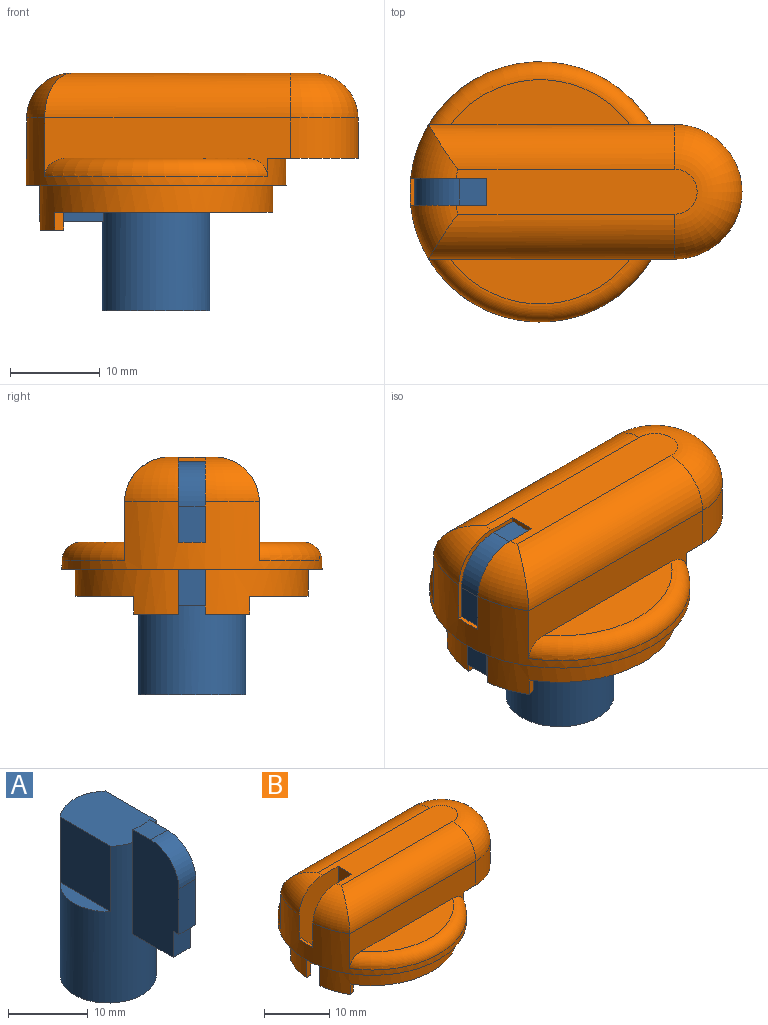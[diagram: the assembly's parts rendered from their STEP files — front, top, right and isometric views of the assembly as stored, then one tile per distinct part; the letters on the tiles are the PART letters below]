
ASSEMBLY  parts=2 mates=1
PART A: 19 faces, bbox 12x20x26 mm
  f0: plane 16x8.19mm, normal (-1,0,0), area 121.7mm2, adj f1,f3,f8,f9,f10,f14,f15,f16
  f1: plane 7x3mm, normal (0,-1,0), area 21mm2, adj f0,f2,f15,f16
  f2: plane 16x8.19mm, normal (1,0,0), area 121.7mm2, adj f1,f3,f8,f9,f10,f14,f15,f16
  f3: cylinder r=6mm len=24mm, axis (0,0,-1), area 660.5mm2, adj f0,f2,f6,f10,f11,f12,f13,f17
  f4: plane 10x4.4mm, normal (0,1,0), area 44mm2, adj f5,f6,f7
  f5: cylinder r=2.95mm len=10mm, axis (0,0,-1), area 135.7mm2, adj f4,f6,f7
  f6: plane 12x12mm, normal (0,0,-1), area 88.8mm2, adj f3,f4,f5
  f7: plane 5.9x4.92mm, normal (0,0,-1), area 24.3mm2, adj f4,f5
  f8: cylinder r=6mm len=3mm, axis (0,0,-1), area 6.1mm2, adj f0,f2,f9,f13
  f9: plane 3.19x3mm, normal (0,0,1), area 9.2mm2, adj f0,f2,f8,f16
  f10: plane 7.19x3mm, normal (0,0,-1), area 21.2mm2, adj f0,f2,f3,f14
  f11: plane 10x8.94mm, normal (1,0,0), area 89.4mm2, adj f3,f13,f18
  f12: plane 10x8.94mm, normal (-1,0,0), area 89.4mm2, adj f3,f13,f17
  f13: plane 12x8mm, normal (0,0,1), area 88.3mm2, adj f3,f8,f11,f12
  f14: plane 4x3mm, normal (0,-1,0), area 12mm2, adj f0,f2,f10,f15
  f15: plane 3x1mm, normal (0,0,-1), area 3mm2, adj f0,f1,f2,f14
  f16: cylinder r=5mm len=5mm, axis (-1,0,0), area 23.6mm2, adj f0,f1,f2,f9
  f17: plane 8.94x2mm, normal (0,0,1), area 12.4mm2, adj f3,f12
  f18: plane 8.94x2mm, normal (0,0,1), area 12.4mm2, adj f3,f11
PART B: 37 faces, bbox 38.1x31.4x17.5 mm
  f0: plane 3x2.5mm, normal (-1,0,0), area 7.5mm2, adj f16,f17,f18,f34
  f1: cylinder r=12mm len=4.67mm, axis (0,0,1), area 9.9mm2, adj f2,f7,f16,f19
  f2: plane 4.97x2.62mm, normal (0,0,-1), area 5.1mm2, adj f1,f6,f16,f19
  f3: plane 3x0.58mm, normal (0,0,1), area 1.5mm2, adj f10,f16,f17,f33
  f4: plane 20x5mm, normal (0,0,1), area 69.9mm2, adj f15,f36
  f5: cylinder r=11.6mm len=23.2mm, axis (0,0,-1), area 209.6mm2, adj f7,f11,f16,f17
  f6: cylinder r=13mm len=26mm, axis (0,0,-1), area 257.1mm2, adj f2,f7,f8,f16,f17,f19,f21,f22
  f7: plane 26x24.91mm, normal (0,0,-1), area 93.7mm2, adj f1,f5,f6,f16,f17,f19,f20,f21
  f8: plane 29x29mm, normal (0,0,-1), area 126.6mm2, adj f6,f10,f16,f17,f33
  f9: plane 20x5mm, normal (0,0,1), area 69.9mm2, adj f13,f35
  f10: cylinder r=14.5mm len=29mm, axis (0,0,-1), area 211.6mm2, adj f3,f8,f12,f13,f15,f16,f17,f23
  f11: plane 23.2x23.1mm, normal (0,0,-1), area 315.8mm2, adj f5,f16,f17,f28,f29,f30,f31,f32
  f12: plane 15x10.09mm, normal (0,0,-1), area 106mm2, adj f10,f13,f14,f15
  f13: plane 27.41x6.5mm, normal (0,-1,0), area 125.4mm2, adj f9,f10,f12,f14,f24,f35
  f14: cylinder r=7.5mm len=15mm, axis (0,0,-1), area 106mm2, adj f12,f13,f15,f26
  f15: plane 27.41x6.5mm, normal (0,1,0), area 125.4mm2, adj f4,f10,f12,f14,f27,f36
  f16: plane 17.5x8.61mm, normal (0,-1,0), area 106.7mm2, adj f0,f1,f2,f3,f5,f6,f7,f8
  f17: plane 17.5x8.61mm, normal (0,1,0), area 106.7mm2, adj f0,f3,f5,f6,f7,f8,f10,f11
  f18: plane 26.88x5mm, normal (0,0,1), area 121.1mm2, adj f0,f16,f17,f23,f24,f25,f26,f27
  f19: plane 2x0.99mm, normal (0.29,0.96,0), area 2.1mm2, adj f1,f2,f6,f7
  f20: cylinder r=12mm len=4.67mm, axis (0,0,1), area 9.9mm2, adj f7,f17,f21,f22
  f21: plane 2x0.99mm, normal (0.29,-0.96,0), area 2.1mm2, adj f6,f7,f20,f22
  f22: plane 4.97x2.62mm, normal (0,0,-1), area 5.1mm2, adj f6,f17,f20,f21
  f23: torus R=9.5mm, axis (0,0,1), area 34.6mm2, adj f10,f17,f18,f24
  f24: cylinder r=5mm len=27.41mm, axis (-1,0,0), area 206.5mm2, adj f13,f18,f23,f26
  f25: torus R=9.5mm, axis (0,0,1), area 34.6mm2, adj f10,f16,f18,f27
  f26: torus R=2.5mm, axis (0,0,1), area 140.2mm2, adj f14,f18,f24,f27
  f27: cylinder r=5mm len=27.41mm, axis (1,0,0), area 206.5mm2, adj f15,f18,f25,f26
  f28: cylinder r=6mm len=10mm, axis (0,0,-1), area 30mm2, adj f11,f17,f32,f34
  f29: cylinder r=6mm len=10mm, axis (0,0,-1), area 30mm2, adj f11,f16,f30,f34
  f30: plane 10x8.76mm, normal (0,-1,0), area 87.6mm2, adj f11,f29,f31,f34
  f31: cylinder r=6mm len=10mm, axis (0,0,-1), area 90.3mm2, adj f11,f30,f32,f34
  f32: plane 10x8.76mm, normal (0,1,0), area 87.6mm2, adj f11,f28,f31,f34
  f33: cylinder r=14mm len=3mm, axis (0,0,-1), area 9mm2, adj f3,f8,f16,f17
  f34: plane 11.92x8.2mm, normal (0,0,-1), area 90mm2, adj f0,f16,f17,f28,f29,f30,f31,f32
  f35: torus R=12.5mm, axis (0,0,1), area 86.1mm2, adj f9,f10,f13
  f36: torus R=12.5mm, axis (0,0,1), area 86.1mm2, adj f4,f10,f15
PLACE A rot(axis=(0,0,-1),90deg) t=(0.1,0,-5.3)mm
PLACE B t=(0.1,0,5.7)mm
MATE parallel A.f3 <-> B.f1  axis (0,0,1) through (0.1,0,18.7)mm
